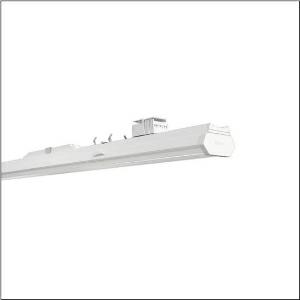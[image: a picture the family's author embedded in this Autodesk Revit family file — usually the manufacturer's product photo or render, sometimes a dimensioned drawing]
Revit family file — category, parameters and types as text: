
# Revit family: licross_r__11_protected_ho_51td13dn4f5s_2531
name_source: partatom
category: Lighting Fixtures
units: mm (PartAtom-declared; Revit-internal decimal feet)

## family parameters
Cut with Voids When Loaded = No
Host = Face
Light Source = No
Part Type = Normal
Room Calculation Point = No
Round Connector Dimension = Use Diameter
Shared = No

## types (1)
- --- (1 x LED, 15550 lm, 87.3 W, 4000K)
    Apparent Load = 87 VA
    CIE Flux Codes = 89 96 99 100 99
    Color Rendering = 80
    Color Temperature = 4000K
    Default Elevation = 1800 mm
    Description = Licross® 11 Protected HO, luminaire insert, of sheet steel, galvanised, coil coated, white, length: 1.500mm, width: 90mm, height: 101mm, LED rated luminous flux: 15.550lm, light colour: 840, control gear: DALI 2, with plug, 5-pole, with phase selection, mains connection: 220..240V, AC, 50/60Hz, rated input power: 87W, halogen-free wiring, primary light control with lens, of plastic, primary optical cover: cover, of PMMA, light emission: direct distribution, primary light characteristic: symmetric, protection rating (complete): IP54, insulation class (complete): insulation class I (protective earthing), certification: CE, ENEC, VDE, UKCA, protection symbol: D if used in an environment with non-conductive dust loads with corresponding accessories, impact resistance: IK06, permissible ambient temperature for indoor applications: -25..+30°C, corresponds to IFS (International Featured Standards) requirements for safety and quality in the food industry, reducing of maximum allowable ambient temperature of 5°C with ceiling mounting, LABS conformity tested according to VDMA 24364:2018-05, packaging unit: 1 piece
    Height = 92 mm
    Lamp = 1 x LED
    Lamp Light Flux = 15550 lm
    Lamp Power = 87.3 W
    Lamp count = 1
    Length = 1500 mm
    Luminous efficacy = 178 lm/W
    Manufacturer = Siteco
    ModVariant = No
    Model = 51TD13DN4F5S
    Mounting Place = Ceiling
    Mounting Type = Pendant
    Number of Poles = 1
    OnlyDefault = Yes
    Power Factor = 1
    Product Name = Licross® 11 Protected HO
    Product group = luminaire insert
    ProductGroupID = 902
    Protection Class = Protection class I
    Protection Degree = IP 54
    RLX_Detail_Level = 1
    RLX_Emergency_Light_Flux = 0 lm
    RLX_Emergency_Type = 0
    RLX_Emergency_Type_DB = No
    RlxData = <blob elided: 24329 chars, md5=d0ee450e>
    Socket = socket
    Standby Power = 0 W
    System Light Flux = 15550 lm
    System Power = 87 W
    Type Comments = factory setting: luminous flux: 100 % | dim-lin: 254 | 589 mA
    Type Image = l_1256145.jpg
    URL = http://relux.com
    VarID = @adj_100930
    Voltage = 0 V
    Weight = 0.00 kg
    Width = 88 mm

## geometry (parser evidence)
native form markers: Blend x4, Sweep x11
no freeform markers — native parametric forms only
